# Revit family: Gewindehaken
name_source: partatom
category: HLS-Bauteile
revit_build: Autodesk Revit 2017 (Build: 20190507_1515(x64)
units: mm (PartAtom-declared; Revit-internal decimal feet)

## family parameters
Arbeitsebenenbasiert = Ja
Beim Laden mit Abzugskörper schneiden = Nein
Bemaßung runder Anschluss = Durchmesser verwenden
Gemeinsam genutzt = Ja
Immer vertikal = Nein
Raumberechnungspunkt = Nein
Teiletyp = Normal

## types (2) — shared parameters
Fabrikat = MEFA
Firma = MEFA Befestigungs- und Montagesysteme GmbH
Kurztext1 = Gewindehaken Trapezblech
L = 113 mm
Länge = 130 mm  [stored 0.426509 ft]
Länge Gewinde = 80 mm  [stored 0.262467 ft]
Länge Haken = 35 mm
Material = Stahl
Mengeneinheit = St
Vorgabe-Ansicht = 1219 mm
vpe = 50 St

## per-type parameters (varying)
| type | Artikelnummer | Breite | D | EAN | Gewicht | Gewicht pro Bauteil | Gewinde | Kurztext2 | max. zul. Last |
| Gewindehaken M 8x130 | 0592131 | 48 mm  [stored 0.15748 ft] | 7 mm  [stored 0.0229659 ft] | 4250928415363 | 0.06 kg | 0.06 kg | M8 | M8 x 130 mm | 0.70 kN |
| Gewindehaken M10x130 | 0592132 | 50 mm  [stored 0.164042 ft] | 8 mm  [stored 0.0262467 ft] | 4250928415370 | 0.09 kg | 0.09 kg | M10 | M10 x 130 mm | 1.30 kN |

note: [stored X ft] marks values corroborated as IEEE doubles in the binary element streams (Revit-internal decimal feet)
